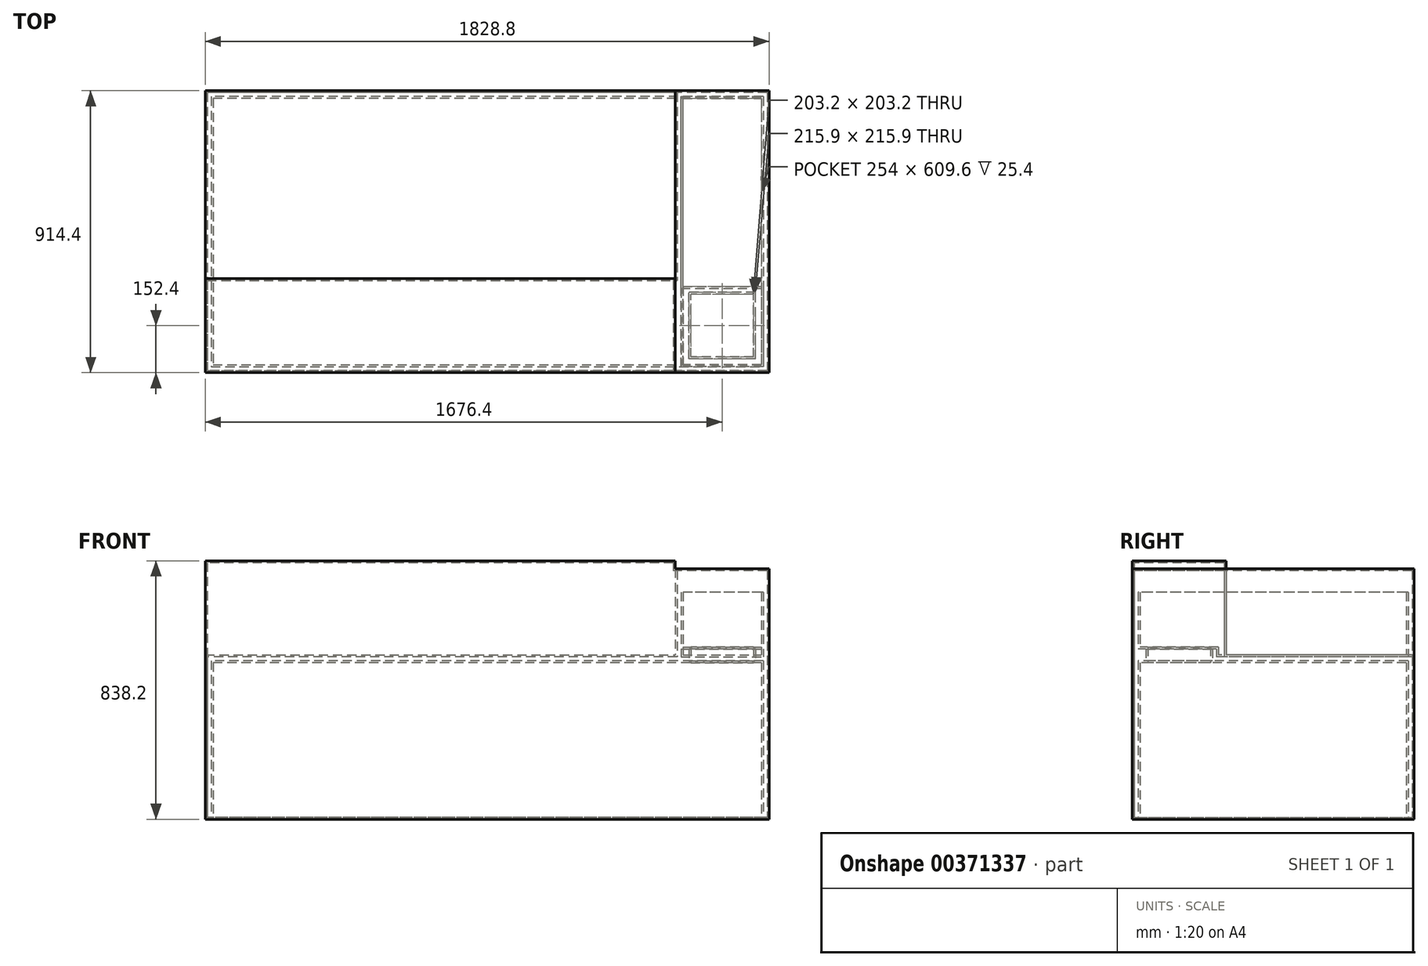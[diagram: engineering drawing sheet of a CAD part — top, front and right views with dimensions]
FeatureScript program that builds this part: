
annotation { "Feature Type Name" : "Feature", "Feature Type Description" : "" }
export const myFeature = defineFeature(function(context is Context, id is Id, definition is map)
    precondition{}
    {
        {
            var Q0;
            Q0=qCreatedBy(makeId("Top.planeOp"),FACE);
            var sketch = newSketch(context, id + "F0", { "sketchPlane" : qUnion([Q0])});
            skLineSegment(sketch, "E0.bottom", {"start": v(0, 0) * mm, "end": v(-1828.8, 0) * mm});
            skLineSegment(sketch, "E0.top", {"start": v(0, -914.4) * mm, "end": v(-1828.8, -914.4) * mm});
            skLineSegment(sketch, "E0.left", {"start": v(0, 0) * mm, "end": v(0, -914.4) * mm});
            skLineSegment(sketch, "E0.right", {"start": v(-1828.8, 0) * mm, "end": v(-1828.8, -914.4) * mm});
            skLineSegment(sketch, "E1.bottom", {"start": v(-254, -660.4) * mm, "end": v(-50.8, -660.4) * mm});
            skLineSegment(sketch, "E1.top", {"start": v(-254, -863.6) * mm, "end": v(-50.8, -863.6) * mm});
            skLineSegment(sketch, "E1.left", {"start": v(-254, -660.4) * mm, "end": v(-254, -863.6) * mm});
            skLineSegment(sketch, "E1.right", {"start": v(-50.8, -660.4) * mm, "end": v(-50.8, -863.6) * mm});
            skSolve(sketch);
        }
        {
            var Q0;
            Q0 = qSketchRegion(id + "F0", true);
            extrude(context, id + "F1", {"entities" : qUnion([Q0]), "depth" : 25.4 * mm});
        }
        {
            var Q0;
            Q0=qCreatedBy(makeId("Top.planeOp"),FACE);
            var sketch = newSketch(context, id + "F2", { "sketchPlane" : qUnion([Q0])});
            skLineSegment(sketch, "E2.0.0", {"start": v(-1828.8, -914.4) * mm, "end": v(0, -914.4) * mm});
            skLineSegment(sketch, "E2.0.1", {"start": v(0, -914.4) * mm, "end": v(0, 0) * mm});
            skLineSegment(sketch, "E2.0.2", {"start": v(0, 0) * mm, "end": v(-1828.8, 0) * mm});
            skLineSegment(sketch, "E2.0.3", {"start": v(-1828.8, 0) * mm, "end": v(-1828.8, -914.4) * mm});
            skSolve(sketch);
        }
        {
            var Q0;
            Q0 = qSketchRegion(id + "F2", true);
            extrude(context, id + "F3", {"entities" : qUnion([Q0]), "operationType" : NewBodyOperationType.ADD, "oppositeDirection" : true, "depth" : 508 * mm});
        }
        {
            var Q0;
            Q0=makeQuery(id+"F3.opExtrude","CAP_FACE",FACE,{"disambiguationData":[OSD([sQuery(id+"F2.wireOp",EDGE,"E2.0.0"),sQuery(id+"F2.wireOp",EDGE,"E2.0.1"),sQuery(id+"F2.wireOp",EDGE,"E2.0.2"),sQuery(id+"F2.wireOp",EDGE,"E2.0.3")])],"isStart":true});
            var Q1;
            Q1=makeQuery(id+"F3.opExtrude","CAP_FACE",FACE,{"disambiguationData":[OSD([sQuery(id+"F2.wireOp",EDGE,"E2.0.0"),sQuery(id+"F2.wireOp",EDGE,"E2.0.1"),sQuery(id+"F2.wireOp",EDGE,"E2.0.2"),sQuery(id+"F2.wireOp",EDGE,"E2.0.3")])],"isStart":false});
            shell(context, id + "F4", {"entities" : qUnion([Q0, Q1]), "thickness" : 25.4 * mm});
        }
        {
            var Q0;
            Q0=makeQuery(id+"F1.opExtrude","CAP_FACE",FACE,{"disambiguationData":[OSD([sQuery(id+"F0.wireOp",EDGE,"E0.bottom"),sQuery(id+"F0.wireOp",EDGE,"E0.top"),sQuery(id+"F0.wireOp",EDGE,"E0.left"),sQuery(id+"F0.wireOp",EDGE,"E0.right"),sQuery(id+"F0.wireOp",EDGE,"E1.bottom"),sQuery(id+"F0.wireOp",EDGE,"E1.top"),sQuery(id+"F0.wireOp",EDGE,"E1.left"),sQuery(id+"F0.wireOp",EDGE,"E1.right")])],"isStart":false});
            var sketch = newSketch(context, id + "F5", { "sketchPlane" : qUnion([Q0])});
            skLineSegment(sketch, "E3.bottom", {"start": v(0, 0) * mm, "end": v(-304.8, 0) * mm});
            skLineSegment(sketch, "E3.top", {"start": v(0, -914.4) * mm, "end": v(-304.8, -914.4) * mm});
            skLineSegment(sketch, "E3.left", {"start": v(0, 0) * mm, "end": v(0, -914.4) * mm});
            skLineSegment(sketch, "E3.right", {"start": v(-304.8, 0) * mm, "end": v(-304.8, -914.4) * mm});
            skSolve(sketch);
        }
        {
            var Q0;
            Q0 = qSketchRegion(id + "F5", true);
            extrude(context, id + "F6", {"entities" : qUnion([Q0]), "operationType" : NewBodyOperationType.ADD, "depth" : 254 * mm});
        }
        {
            var Q0;
            Q0=makeQuery(id+"F6.opExtrude","CAP_FACE",FACE,{"disambiguationData":[OSD([sQuery(id+"F5.wireOp",EDGE,"E3.bottom"),sQuery(id+"F5.wireOp",EDGE,"E3.top"),sQuery(id+"F5.wireOp",EDGE,"E3.left"),sQuery(id+"F5.wireOp",EDGE,"E3.right")])],"isStart":false});
            shell(context, id + "F7", {"entities" : qUnion([Q0]), "thickness" : 25.4 * mm});
        }
        {
            var Q0;
            Q0=makeQuery(id+"F6.opExtrude","CAP_FACE",FACE,{"disambiguationData":[OSD([sQuery(id+"F5.wireOp",EDGE,"E3.bottom"),sQuery(id+"F5.wireOp",EDGE,"E3.top"),sQuery(id+"F5.wireOp",EDGE,"E3.left"),sQuery(id+"F5.wireOp",EDGE,"E3.right")])],"isStart":true});
            extrude(context, id + "F8", {"entities" : qUnion([Q0]), "operationType" : NewBodyOperationType.REMOVE, "oppositeDirection" : true, "depth" : 50.8 * mm});
        }
        {
            var Q0;
            Q0=makeQuery(id+"F1.opExtrude","CAP_FACE",FACE,{"disambiguationData":[OSD([sQuery(id+"F0.wireOp",EDGE,"E0.bottom"),sQuery(id+"F0.wireOp",EDGE,"E0.top"),sQuery(id+"F0.wireOp",EDGE,"E0.left"),sQuery(id+"F0.wireOp",EDGE,"E0.right"),sQuery(id+"F0.wireOp",EDGE,"E1.bottom"),sQuery(id+"F0.wireOp",EDGE,"E1.top"),sQuery(id+"F0.wireOp",EDGE,"E1.left"),sQuery(id+"F0.wireOp",EDGE,"E1.right")])],"isStart":false});
            var sketch = newSketch(context, id + "F9", { "sketchPlane" : qUnion([Q0])});
            skLineSegment(sketch, "E4.bottom", {"start": v(-1828.8, -914.4) * mm, "end": v(-304.8, -914.4) * mm});
            skLineSegment(sketch, "E4.top", {"start": v(-1828.8, -609.6) * mm, "end": v(-304.8, -609.6) * mm});
            skLineSegment(sketch, "E4.left", {"start": v(-1828.8, -914.4) * mm, "end": v(-1828.8, -609.6) * mm});
            skLineSegment(sketch, "E4.right", {"start": v(-304.8, -914.4) * mm, "end": v(-304.8, -609.6) * mm});
            skSolve(sketch);
        }
        {
            var Q0;
            Q0 = qSketchRegion(id + "F9", true);
            extrude(context, id + "F10", {"entities" : qUnion([Q0]), "operationType" : NewBodyOperationType.ADD, "depth" : 304.8 * mm});
        }
        {
            var Q0;
            Q0=makeQuery(id+"F6.opExtrude","CAP_FACE",FACE,{"disambiguationData":[OSD([sQuery(id+"F5.wireOp",EDGE,"E3.bottom"),sQuery(id+"F5.wireOp",EDGE,"E3.top"),sQuery(id+"F5.wireOp",EDGE,"E3.left"),sQuery(id+"F5.wireOp",EDGE,"E3.right")])],"isStart":false});
            var sketch = newSketch(context, id + "F11", { "sketchPlane" : qUnion([Q0])});
            skLineSegment(sketch, "E5.0.0", {"start": v(0, 0) * mm, "end": v(-304.8, 0) * mm});
            skLineSegment(sketch, "E5.0.1", {"start": v(-304.8, 0) * mm, "end": v(-304.8, -609.6) * mm});
            skLineSegment(sketch, "E5.0.2", {"start": v(-304.8, -609.6) * mm, "end": v(-304.8, -914.4) * mm});
            skLineSegment(sketch, "E5.0.3", {"start": v(-304.8, -914.4) * mm, "end": v(0, -914.4) * mm});
            skLineSegment(sketch, "E5.0.4", {"start": v(0, -914.4) * mm, "end": v(0, 0) * mm});
            skSolve(sketch);
        }
        {
            var Q0;
            Q0 = qSketchRegion(id + "F11", true);
            extrude(context, id + "F12", {"entities" : qUnion([Q0]), "depth" : 25.4 * mm});
        }
        {
            var Q0;
            Q0=makeQuery(id+"F12.opExtrude","CAP_FACE",FACE,{"disambiguationData":[OSD([sQuery(id+"F11.wireOp",EDGE,"E5.0.0"),sQuery(id+"F11.wireOp",EDGE,"E5.0.1"),sQuery(id+"F11.wireOp",EDGE,"E5.0.2"),sQuery(id+"F11.wireOp",EDGE,"E5.0.3"),sQuery(id+"F11.wireOp",EDGE,"E5.0.4")])],"isStart":true});
            var sketch = newSketch(context, id + "F13", { "sketchPlane" : qUnion([Q0])});
            skLineSegment(sketch, "E6.0", {"start": v(-25.4, 25.4) * mm, "end": v(-25.4, 889) * mm});
            skLineSegment(sketch, "E6.1", {"start": v(-279.4, 25.4) * mm, "end": v(-25.4, 25.4) * mm});
            skLineSegment(sketch, "E6.2", {"start": v(-279.4, 889) * mm, "end": v(-279.4, 25.4) * mm});
            skLineSegment(sketch, "E6.3", {"start": v(-25.4, 889) * mm, "end": v(-279.4, 889) * mm});
            skSolve(sketch);
        }
        {
            var Q0;
            Q0=makeQuery(id+"F13.imprint","IMPRINT",FACE,{"disambiguationData":[TD([[makeQuery(id+"F13.imprint","IMPRINT",EDGE,{"derivedFrom":sQuery(id+"F13.wireOp",EDGE,"E6.0")}),1.0]])]});
            extrude(context, id + "F14", {"entities" : qUnion([Q0]), "operationType" : NewBodyOperationType.ADD, "depth" : 50.8 * mm});
        }
        {
            var Q0;
            Q0=makeQuery(id+"F14.opExtrude","CAP_FACE",FACE,{"disambiguationData":[OSD([sQuery(id+"F13.wireOp",EDGE,"E6.0"),sQuery(id+"F13.wireOp",EDGE,"E6.1"),sQuery(id+"F13.wireOp",EDGE,"E6.2"),sQuery(id+"F13.wireOp",EDGE,"E6.3")])],"isStart":false});
            shell(context, id + "F15", {"entities" : qUnion([Q0]), "thickness" : 6.35 * mm});
        }
    });
